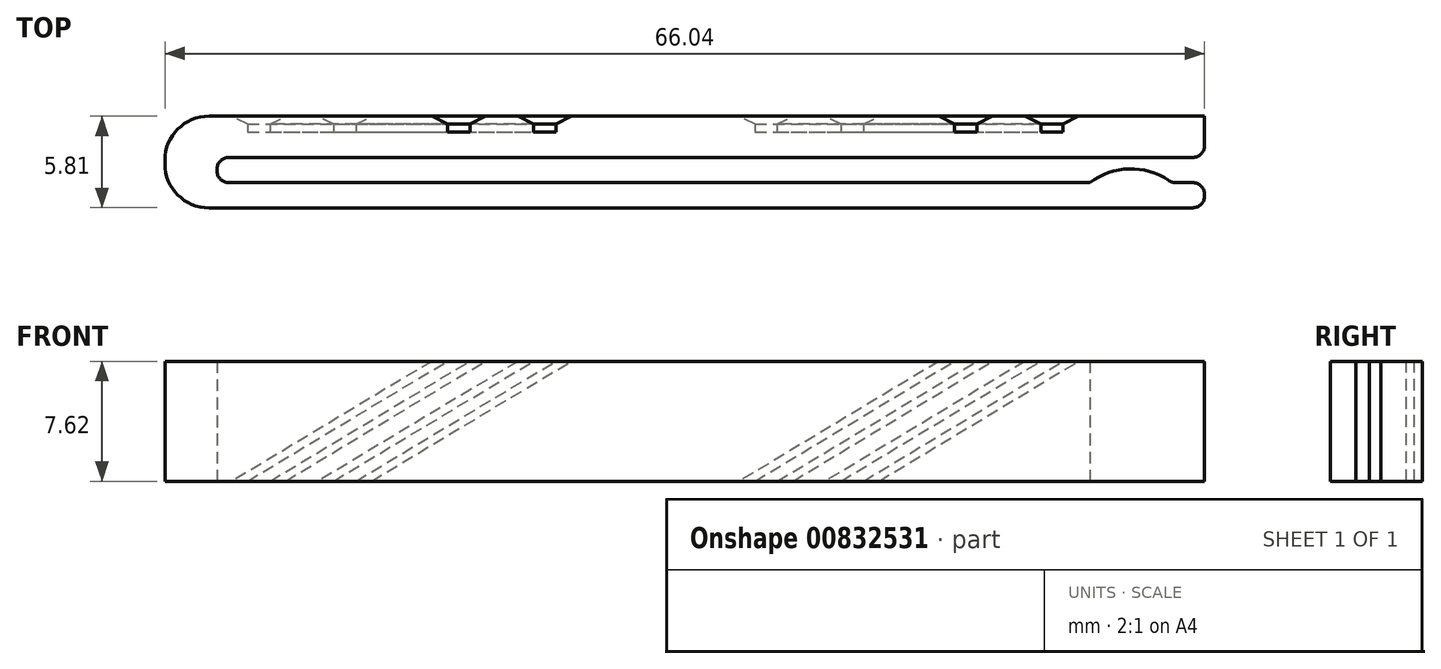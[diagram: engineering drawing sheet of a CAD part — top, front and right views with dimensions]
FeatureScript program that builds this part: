
annotation { "Feature Type Name" : "Feature", "Feature Type Description" : "" }
export const myFeature = defineFeature(function(context is Context, id is Id, definition is map)
    precondition{}
    {
        {
            var Q0;
            Q0=qCreatedBy(makeId("Top.planeOp"),FACE);
            var sketch = newSketch(context, id + "F0", { "sketchPlane" : qUnion([Q0])});
            skLineSegment(sketch, "E0", {"start": v(-3.86, 9.14) * mm, "end": v(62.18, 9.14) * mm});
            skLineSegment(sketch, "E1", {"start": v(62.18, 7.54) * mm, "end": v(-0.56, 7.54) * mm});
            skLineSegment(sketch, "E2", {"start": v(-0.56, 5.94) * mm, "end": v(54.89, 5.94) * mm});
            skLineSegment(sketch, "E3", {"start": v(62.18, 4.35) * mm, "end": v(-3.86, 4.35) * mm});
            skLineSegment(sketch, "E4", {"start": v(-3.86, 4.35) * mm, "end": v(-3.86, 9.14) * mm});
            skPoint(sketch, "E5.visualSharp", {"position": v(-3.86, 9.14) * mm});
            skPoint(sketch, "E6.visualSharp", {"position": v(-3.86, 4.35) * mm});
            skArc(sketch, "E7", {"start": v(60.09, 5.94) * mm, "mid": v(57.49, 6.82) * mm, "end": v(54.89, 5.94) * mm});
            skLineSegment(sketch, "E8", {"start": v(62.18, 4.35) * mm, "end": v(62.18, 5.94) * mm});
            skLineSegment(sketch, "E9", {"start": v(60.09, 5.94) * mm, "end": v(62.18, 5.94) * mm});
            skLineSegment(sketch, "E10.0", {"start": v(-0.56, 5.94) * mm, "end": v(-0.56, 7.54) * mm});
            skLineSegment(sketch, "E11.trimOffspring", {"start": v(62.18, 7.54) * mm, "end": v(62.18, 9.14) * mm});
            skSolve(sketch);
        }
        {
            var Q0;
            Q0=makeQuery(id+"F0.imprint","IMPRINT",FACE,{"disambiguationData":[TD([[makeQuery(id+"F0.imprint","IMPRINT",EDGE,{"derivedFrom":sQuery(id+"F0.wireOp",EDGE,"E0")}),-1.0]])]});
            extrude(context, id + "F1", {"entities" : qUnion([Q0]), "depth" : 7.62 * mm, "offsetDistance" : 25.4 * mm});
        }
        {
            var Q0;
            Q0=makeQuery(id+"F1.opExtrude","SWEPT_FACE",FACE,{"disambiguationData":[OSD([sQuery(id+"F0.wireOp",EDGE,"E0")])]});
            var sketch = newSketch(context, id + "F2", { "sketchPlane" : qUnion([Q0])});
            skLineSegment(sketch, "E12.0", {"start": v(3.86, 0) * mm, "end": v(3.86, 0) * mm});
            skLineSegment(sketch, "E12.1", {"start": v(3.86, 7.62) * mm, "end": v(3.86, 7.62) * mm});
            skLineSegment(sketch, "E13", {"start": v(-6.85, 0) * mm, "end": v(-19.55, 7.62) * mm});
            skLineSegment(sketch, "E14", {"start": v(-8.28, 0) * mm, "end": v(-20.97, 7.62) * mm});
            skLineSegment(sketch, "E15", {"start": v(-1.4, 0) * mm, "end": v(-14.09, 7.62) * mm});
            skLineSegment(sketch, "E16", {"start": v(-2.82, 0) * mm, "end": v(-15.51, 7.62) * mm});
            skLineSegment(sketch, "E17", {"start": v(-39.07, 0) * mm, "end": v(-51.76, 7.62) * mm});
            skLineSegment(sketch, "E18", {"start": v(-40.5, 0) * mm, "end": v(-53.19, 7.62) * mm});
            skLineSegment(sketch, "E19", {"start": v(-33.6, 0) * mm, "end": v(-46.3, 7.62) * mm});
            skLineSegment(sketch, "E20", {"start": v(-35.03, 0) * mm, "end": v(-47.73, 7.62) * mm});
            skSolve(sketch);
        }
        {
            var Q0;
            {var subQ2=sQuery(id+"F2.wireOp",EDGE,"E15");Q0=makeQuery(id+"F2.imprint","IMPRINT",FACE,{"disambiguationData":[TD([[makeQuery(id+"F2.imprint","IMPRINT",EDGE,{"derivedFrom":subQ2}),-1.0]])]});}
            var Q1;
            {var subQ0=sQuery(id+"F2.wireOp",EDGE,"E13");Q1=makeQuery(id+"F2.imprint","IMPRINT",FACE,{"disambiguationData":[TD([[makeQuery(id+"F2.imprint","IMPRINT",EDGE,{"derivedFrom":subQ0}),-1.0]])]});}
            var Q2;
            {var subQ0=sQuery(id+"F2.wireOp",EDGE,"E14");Q2=makeQuery(id+"F2.imprint","IMPRINT",FACE,{"disambiguationData":[TD([[makeQuery(id+"F2.imprint","IMPRINT",EDGE,{"derivedFrom":subQ0}),1.0]])]});}
            var Q3;
            {var subQ0=sQuery(id+"F2.wireOp",EDGE,"E17");Q3=makeQuery(id+"F2.imprint","IMPRINT",FACE,{"disambiguationData":[TD([[makeQuery(id+"F2.imprint","IMPRINT",EDGE,{"derivedFrom":subQ0}),-1.0]])]});}
            var Q4;
            {var subQ2=sQuery(id+"F2.wireOp",EDGE,"E18");Q4=makeQuery(id+"F2.imprint","IMPRINT",FACE,{"disambiguationData":[TD([[makeQuery(id+"F2.imprint","IMPRINT",EDGE,{"derivedFrom":subQ2}),1.0]])]});}
            extrude(context, id + "F3", {"entities" : qUnion([Q0, Q1, Q2, Q3, Q4]), "operationType" : NewBodyOperationType.ADD, "depth" : 1.02 * mm, "offsetDistance" : 25.4 * mm});
        }
        {
            var Q0;
            Q0=makeQuery(id+"F3.opExtrude","CAP_EDGE",EDGE,{"disambiguationData":[OSD([sQuery(id+"F0.wireOp",EDGE,"E0"),sQuery(id+"F0.wireOp",EDGE,"E4")])],"isStart":false});
            var Q1;
            Q1=makeQuery(id+"F1.opExtrude","SWEPT_EDGE",EDGE,{"disambiguationData":[OSD([sQuery(id+"F0.wireOp",EDGE,"E3"),sQuery(id+"F0.wireOp",EDGE,"E4")])]});
            fillet(context, id + "F4", {"entities" : qUnion([Q0, Q1]), "radius" : 2.8 * mm, "tangentPropagation" : true, "allowEdgeOverflow" : false});
        }
        {
            var Q0;
            Q0=makeQuery(id+"F1.opExtrude","SWEPT_EDGE",EDGE,{"disambiguationData":[OSD([sQuery(id+"F0.wireOp",EDGE,"E2"),sQuery(id+"F0.wireOp",EDGE,"E10.0")])]});
            var Q1;
            Q1=makeQuery(id+"F1.opExtrude","SWEPT_EDGE",EDGE,{"disambiguationData":[OSD([sQuery(id+"F0.wireOp",EDGE,"E1"),sQuery(id+"F0.wireOp",EDGE,"E10.0")])]});
            fillet(context, id + "F5", {"entities" : qUnion([Q0, Q1]), "radius" : 0.76 * mm, "tangentPropagation" : true, "allowEdgeOverflow" : false});
        }
        {
            var Q0;
            Q0=makeQuery(id+"F1.opExtrude","SWEPT_EDGE",EDGE,{"disambiguationData":[OSD([sQuery(id+"F0.wireOp",EDGE,"4eDZza3g-Jcoa-xuKd-ygXB-gT2H9ikuJ3zW"),sQuery(id+"F0.wireOp",EDGE,"E9")])]});
            var Q1;
            Q1=makeQuery(id+"F1.opExtrude","SWEPT_EDGE",EDGE,{"disambiguationData":[OSD([sQuery(id+"F0.wireOp",EDGE,"E3"),sQuery(id+"F0.wireOp",EDGE,"4eDZza3g-Jcoa-xuKd-ygXB-gT2H9ikuJ3zW")])]});
            var Q2;
            Q2=makeQuery(id+"F1.opExtrude","SWEPT_EDGE",EDGE,{"disambiguationData":[OSD([sQuery(id+"F0.wireOp",EDGE,"E1"),sQuery(id+"F0.wireOp",EDGE,"E8")])]});
            fillet(context, id + "F6", {"entities" : qUnion([Q0, Q1, Q2]), "radius" : 0.76 * mm, "tangentPropagation" : true, "allowEdgeOverflow" : false});
        }
        {
            var Q0;
            Q0=makeQuery(id+"F3.opExtrude","CAP_EDGE",EDGE,{"disambiguationData":[OSD([sQuery(id+"F2.wireOp",EDGE,"E15")])],"isStart":false});
            var Q1;
            Q1=makeQuery(id+"F3.opExtrude","CAP_EDGE",EDGE,{"disambiguationData":[OSD([sQuery(id+"F2.wireOp",EDGE,"E16")])],"isStart":false});
            var Q2;
            Q2=makeQuery(id+"F3.opExtrude","CAP_EDGE",EDGE,{"disambiguationData":[OSD([sQuery(id+"F2.wireOp",EDGE,"E13")])],"isStart":false});
            var Q3;
            Q3=makeQuery(id+"F3.opExtrude","CAP_EDGE",EDGE,{"disambiguationData":[OSD([sQuery(id+"F2.wireOp",EDGE,"E14")])],"isStart":false});
            var Q4;
            Q4=makeQuery(id+"F3.opExtrude","CAP_EDGE",EDGE,{"disambiguationData":[OSD([sQuery(id+"F2.wireOp",EDGE,"E19")])],"isStart":false});
            var Q5;
            Q5=makeQuery(id+"F3.opExtrude","CAP_EDGE",EDGE,{"disambiguationData":[OSD([sQuery(id+"F2.wireOp",EDGE,"E20")])],"isStart":false});
            var Q6;
            Q6=makeQuery(id+"F3.opExtrude","CAP_EDGE",EDGE,{"disambiguationData":[OSD([sQuery(id+"F2.wireOp",EDGE,"E17")])],"isStart":false});
            var Q7;
            Q7=makeQuery(id+"F3.opExtrude","CAP_EDGE",EDGE,{"disambiguationData":[OSD([sQuery(id+"F2.wireOp",EDGE,"E18")])],"isStart":false});
            chamfer(context, id + "F7", {"entities" : qUnion([Q0, Q1, Q2, Q3, Q4, Q5, Q6, Q7]), "width" : 0.5 * mm, "tangentPropagation" : true});
        }
    });
